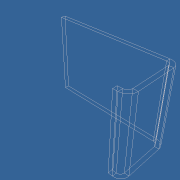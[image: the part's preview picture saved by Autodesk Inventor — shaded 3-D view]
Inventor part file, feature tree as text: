
AUTODESK INVENTOR PART (.ipt)
format: ipt  version: unknown  size: 195,584 bytes
history: native  units: mm
features: sheet_metal_op x7, sketch x3, other x3
ambient origin geometry x8: Origin, YZ Plane, XZ Plane, XY Plane, X Axis, Y Axis, Z Axis, Center Point
bodies: Solid1 (feature_tree)
feature tree (13):
  sheet_metal_op  "Face1"
  sheet_metal_op  "Flange1"
  sheet_metal_op  "Flange2"
  sketch  "Sketch1"  dims[d0=13.0mm]
  other  "Plate1"
  sketch  "Sketch2"  dims[d1=9.0mm]
  other  "Plate2"
  sheet_metal_op  "Bend1"
  sheet_metal_op  "Corner1"
  sketch  "Sketch3"  dims[d2=0.5mm d3=0.5mm d4=0.25mm d5=1.0mm d6=0.5mm d7=5.5mm d8=90.0deg d9=0.5mm d10=2.0mm d11=0.5mm d12=0.5mm d13=0.5mm d14=0.25mm d15=1.0mm d16=0.5mm d17=1.5mm d18=90.0deg d19=0.5mm d20=2.0mm d21=0.5mm d22=0.5mm]
  other  "Plate3"
  sheet_metal_op  "Bend2"
  sheet_metal_op  "Corner2"
